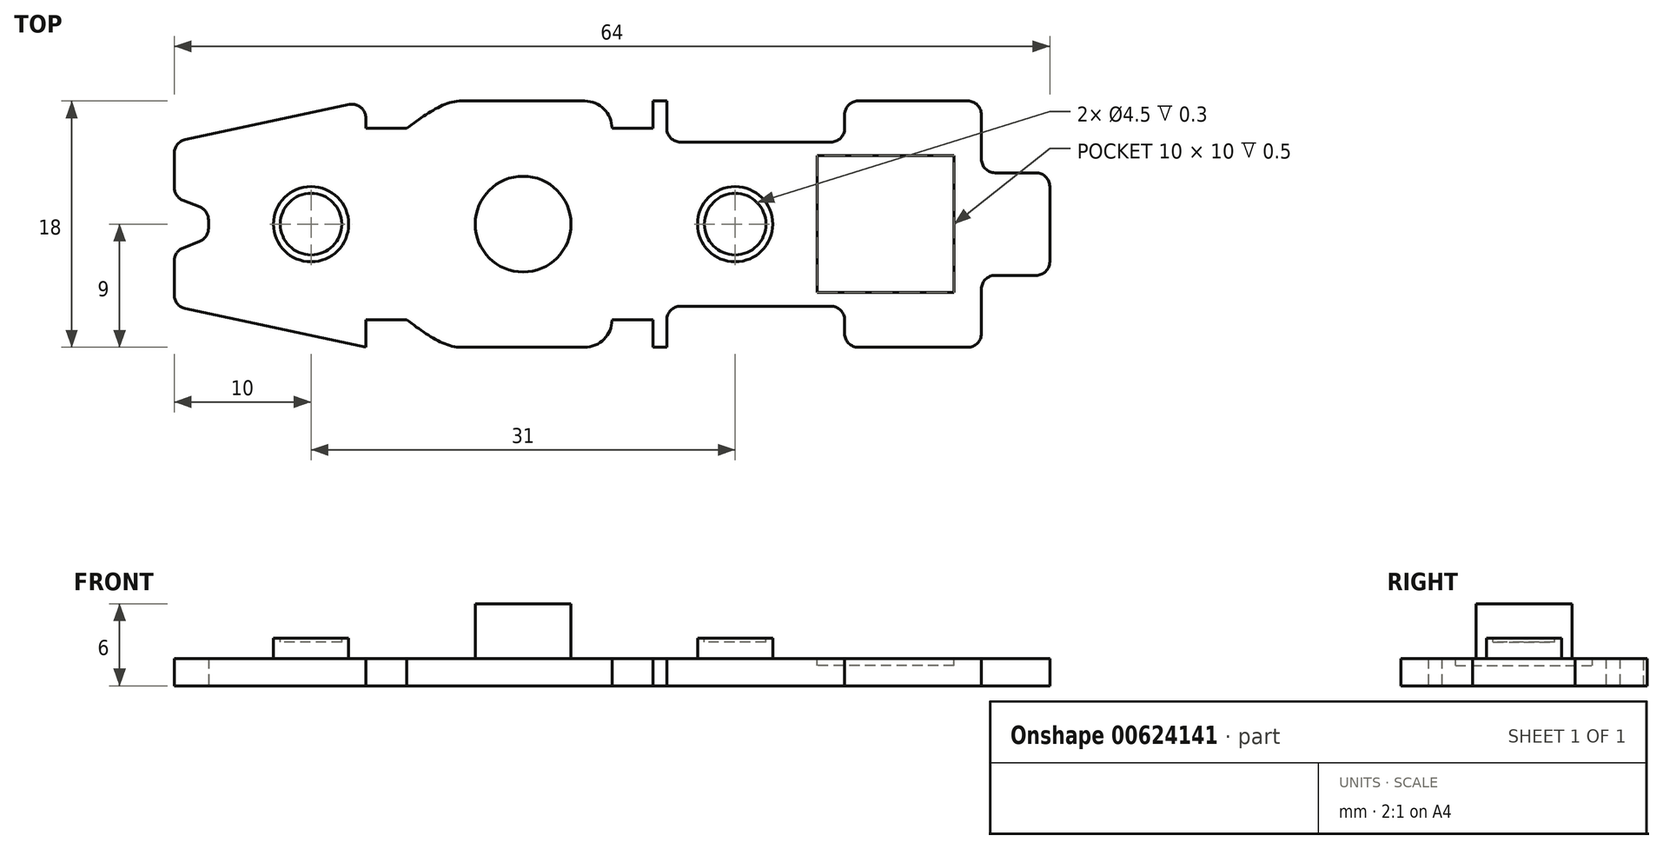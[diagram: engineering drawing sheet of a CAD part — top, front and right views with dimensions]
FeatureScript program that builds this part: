
annotation { "Feature Type Name" : "Feature", "Feature Type Description" : "" }
export const myFeature = defineFeature(function(context is Context, id is Id, definition is map)
    precondition{}
    {
        {
            var Q0;
            Q0=qCreatedBy(makeId("Top.planeOp"),FACE);
            var sketch = newSketch(context, id + "F0", { "sketchPlane" : qUnion([Q0])});
            skLineSegment(sketch, "E0.bottom", {"start": v(27, 9) * mm, "end": v(17, 9) * mm});
            skLineSegment(sketch, "E0.left", {"start": v(32, 3.75) * mm, "end": v(32, 0) * mm});
            skLineSegment(sketch, "E0.right", {"start": v(-32, 6) * mm, "end": v(-32, 2) * mm});
            skPoint(sketch, "E0.middle", {"position": v(0, 0) * mm});
            skLineSegment(sketch, "E1", {"start": v(32, 0) * mm, "end": v(32, 3.75) * mm});
            skLineSegment(sketch, "E2", {"start": v(32, 3.75) * mm, "end": v(28, 3.75) * mm});
            skLineSegment(sketch, "E3", {"start": v(27, 4.75) * mm, "end": v(27, 9) * mm});
            skPoint(sketch, "E4.orphan", {"position": v(32, 9) * mm});
            skLineSegment(sketch, "E5", {"start": v(17, 9) * mm, "end": v(17, 7) * mm});
            skLineSegment(sketch, "E6", {"start": v(16, 6) * mm, "end": v(5, 6) * mm});
            skLineSegment(sketch, "E7", {"start": v(4, 7) * mm, "end": v(4, 9) * mm});
            skLineSegment(sketch, "E8", {"start": v(4, 9) * mm, "end": v(3, 9) * mm});
            skLineSegment(sketch, "E9", {"start": v(3, 9) * mm, "end": v(3, 7) * mm});
            skLineSegment(sketch, "E10", {"start": v(3, 7) * mm, "end": v(0, 7) * mm});
            skPoint(sketch, "E11.start.orphan", {"position": v(-2, 7) * mm});
            skArc(sketch, "E12", {"start": v(-2, 9) * mm, "mid": v(-0.59, 8.41) * mm, "end": v(0, 7) * mm});
            skLineSegment(sketch, "E13.trimOffspring", {"start": v(-2, 9) * mm, "end": v(-11, 9) * mm});
            skPoint(sketch, "E14.orphan", {"position": v(0, 9) * mm});
            skFitSpline(sketch, "E15", {"points": [v(-15, 7) * mm, v(-11, 9) * mm, v(-7, 7) * mm], "startDerivative": vector(8, 6) * mm, "endDerivative": vector(8, -6) * mm});
            skLineSegment(sketch, "E16", {"start": v(-15, 7) * mm, "end": v(-18, 7) * mm});
            skLineSegment(sketch, "E17", {"start": v(-18, 7) * mm, "end": v(-18, 9) * mm});
            skLineSegment(sketch, "E18", {"start": v(-32, 2) * mm, "end": v(-32, 6) * mm});
            skLineSegment(sketch, "E19", {"start": v(-32, 6) * mm, "end": v(-18, 9) * mm});
            skLineSegment(sketch, "E20", {"start": v(-29.5, 0) * mm, "end": v(-29.5, 0.32) * mm});
            skLineSegment(sketch, "E21", {"start": v(-32, 2) * mm, "end": v(-30.13, 1.25) * mm});
            skPoint(sketch, "E22.orphan", {"position": v(-32, 9) * mm});
            skPoint(sketch, "E23.trimOffspring.start.orphan", {"position": v(-32, 0) * mm});
            skPoint(sketch, "E0.top.end.orphan", {"position": v(-32, -9) * mm});
            skPoint(sketch, "E24.orphan", {"position": v(32, -9) * mm});
            skLineSegment(sketch, "E25.MirrorCS", {"start": v(-29.5, 0) * mm, "end": v(-29.5, -0.32) * mm});
            skLineSegment(sketch, "E26.MirrorCS", {"start": v(-31.37, -1.75) * mm, "end": v(-30.13, -1.25) * mm});
            skLineSegment(sketch, "E27.MirrorCS", {"start": v(-32, -2.68) * mm, "end": v(-32, -5.2) * mm});
            skLineSegment(sketch, "E28.MirrorCS", {"start": v(-31.2, -6.17) * mm, "end": v(-18, -9) * mm});
            skLineSegment(sketch, "E29.MirrorCS", {"start": v(-18, -7) * mm, "end": v(-18, -9) * mm});
            skLineSegment(sketch, "E30.MirrorCS", {"start": v(-15, -7) * mm, "end": v(-18, -7) * mm});
            skFitSpline(sketch, "E31.MirrorCS", {"points": [v(-15, -7) * mm, v(-11, -9) * mm, v(-7, -7) * mm], "startDerivative": vector(8, -6) * mm, "endDerivative": vector(8, 6) * mm});
            skLineSegment(sketch, "E32.MirrorCS", {"start": v(-2, -9) * mm, "end": v(-11, -9) * mm});
            skArc(sketch, "E33.MirrorCS", {"start": v(-2, -9) * mm, "mid": v(-0.59, -8.41) * mm, "end": v(0, -7) * mm});
            skLineSegment(sketch, "E34.MirrorCS", {"start": v(3, -7) * mm, "end": v(0, -7) * mm});
            skLineSegment(sketch, "E35.MirrorCS", {"start": v(3, -9) * mm, "end": v(3, -7) * mm});
            skLineSegment(sketch, "E36.MirrorCS", {"start": v(4, -9) * mm, "end": v(3, -9) * mm});
            skLineSegment(sketch, "E37.MirrorCS", {"start": v(4, -7) * mm, "end": v(4, -9) * mm});
            skLineSegment(sketch, "E38.MirrorCS", {"start": v(16, -6) * mm, "end": v(5, -6) * mm});
            skLineSegment(sketch, "E39.MirrorCS", {"start": v(17, -8) * mm, "end": v(17, -7) * mm});
            skLineSegment(sketch, "E40.MirrorCS", {"start": v(26, -9) * mm, "end": v(18, -9) * mm});
            skLineSegment(sketch, "E41.MirrorCS", {"start": v(27, -4.75) * mm, "end": v(27, -8) * mm});
            skLineSegment(sketch, "E42.MirrorCS", {"start": v(32, -3.75) * mm, "end": v(28, -3.75) * mm});
            skLineSegment(sketch, "E43.MirrorCS", {"start": v(32, 0) * mm, "end": v(32, -3.75) * mm});
            skPoint(sketch, "E44.end.orphan", {"position": v(-29.5, 2) * mm});
            skPoint(sketch, "E45.visualSharp", {"position": v(27, 3.75) * mm});
            skArc(sketch, "E45.filletArc", {"start": v(27, 4.75) * mm, "mid": v(27.3, 4.04) * mm, "end": v(28, 3.75) * mm});
            skPoint(sketch, "E46.visualSharp", {"position": v(27, -3.75) * mm});
            skArc(sketch, "E46.filletArc", {"start": v(28, -3.75) * mm, "mid": v(27.3, -4.04) * mm, "end": v(27, -4.75) * mm});
            skPoint(sketch, "E47.visualSharp", {"position": v(-29.5, 1) * mm});
            skArc(sketch, "E47.filletArc", {"start": v(-29.5, 0.32) * mm, "mid": v(-29.67, 0.88) * mm, "end": v(-30.13, 1.25) * mm});
            skPoint(sketch, "E48.visualSharp", {"position": v(-29.5, -1) * mm});
            skArc(sketch, "E48.filletArc", {"start": v(-30.13, -1.25) * mm, "mid": v(-29.67, -0.88) * mm, "end": v(-29.5, -0.32) * mm});
            skPoint(sketch, "E49.visualSharp", {"position": v(-32, -2) * mm});
            skArc(sketch, "E49.filletArc", {"start": v(-31.37, -1.75) * mm, "mid": v(-31.83, -2.12) * mm, "end": v(-32, -2.68) * mm});
            skPoint(sketch, "E50.visualSharp", {"position": v(-32, -6) * mm});
            skArc(sketch, "E50.filletArc", {"start": v(-32, -5.2) * mm, "mid": v(-31.78, -5.82) * mm, "end": v(-31.2, -6.17) * mm});
            skPoint(sketch, "E51.visualSharp", {"position": v(4, 6) * mm});
            skArc(sketch, "E51.filletArc", {"start": v(4, 7) * mm, "mid": v(4.3, 6.3) * mm, "end": v(5, 6) * mm});
            skPoint(sketch, "E52.visualSharp", {"position": v(4, -6) * mm});
            skArc(sketch, "E52.filletArc", {"start": v(5, -6) * mm, "mid": v(4.3, -6.3) * mm, "end": v(4, -7) * mm});
            skPoint(sketch, "E53.visualSharp", {"position": v(17, -6) * mm});
            skArc(sketch, "E53.filletArc", {"start": v(17, -7) * mm, "mid": v(16.7, -6.3) * mm, "end": v(16, -6) * mm});
            skPoint(sketch, "E54.visualSharp", {"position": v(17, 6) * mm});
            skArc(sketch, "E54.filletArc", {"start": v(16, 6) * mm, "mid": v(16.7, 6.3) * mm, "end": v(17, 7) * mm});
            skPoint(sketch, "E55.visualSharp", {"position": v(17, -9) * mm});
            skArc(sketch, "E55.filletArc", {"start": v(17, -8) * mm, "mid": v(17.3, -8.7) * mm, "end": v(18, -9) * mm});
            skPoint(sketch, "E56.visualSharp", {"position": v(27, -9) * mm});
            skArc(sketch, "E56.filletArc", {"start": v(26, -9) * mm, "mid": v(26.7, -8.7) * mm, "end": v(27, -8) * mm});
            skSolve(sketch);
        }
        {
            var Q0;
            Q0 = qSketchRegion(id + "F0", true);
            extrude(context, id + "F1", {"entities" : qUnion([Q0]), "depth" : 2 * mm, "offsetDistance" : 25 * mm});
        }
        {
            var Q0;
            Q0=makeQuery(id+"F1.opExtrude","SWEPT_EDGE",EDGE,{"disambiguationData":[OSD([sQuery(id+"F0.wireOp",EDGE,"E18"),sQuery(id+"F0.wireOp",EDGE,"E21")])]});
            var Q1;
            Q1=makeQuery(id+"F1.opExtrude","SWEPT_EDGE",EDGE,{"disambiguationData":[OSD([sQuery(id+"F0.wireOp",EDGE,"E18"),sQuery(id+"F0.wireOp",EDGE,"E19")])]});
            var Q2;
            Q2=makeQuery(id+"F1.opExtrude","SWEPT_EDGE",EDGE,{"disambiguationData":[OSD([sQuery(id+"F0.wireOp",EDGE,"E3"),sQuery(id+"F0.wireOp",EDGE,"E0.bottom")])]});
            var Q3;
            Q3=makeQuery(id+"F1.opExtrude","SWEPT_EDGE",EDGE,{"disambiguationData":[OSD([sQuery(id+"F0.wireOp",EDGE,"E0.bottom"),sQuery(id+"F0.wireOp",EDGE,"E5")])]});
            var Q4;
            Q4=makeQuery(id+"F1.opExtrude","SWEPT_EDGE",EDGE,{"disambiguationData":[OSD([sQuery(id+"F0.wireOp",EDGE,"E42.MirrorCS"),sQuery(id+"F0.wireOp",EDGE,"E43.MirrorCS")])]});
            var Q5;
            Q5=makeQuery(id+"F1.opExtrude","SWEPT_EDGE",EDGE,{"disambiguationData":[OSD([sQuery(id+"F0.wireOp",EDGE,"E1"),sQuery(id+"F0.wireOp",EDGE,"E2")])]});
            fillet(context, id + "F2", {"entities" : qUnion([Q0, Q1, Q2, Q3, Q4, Q5]), "radius" : 1 * mm, "tangentPropagation" : true, "allowEdgeOverflow" : false});
        }
        {
            var Q0;
            Q0=makeQuery(id+"F1.opExtrude","CAP_FACE",FACE,{"disambiguationData":[OSD([sQuery(id+"F0.wireOp",EDGE,"E1"),sQuery(id+"F0.wireOp",EDGE,"E2"),sQuery(id+"F0.wireOp",EDGE,"E3"),sQuery(id+"F0.wireOp",EDGE,"E0.bottom"),sQuery(id+"F0.wireOp",EDGE,"E5"),sQuery(id+"F0.wireOp",EDGE,"E6"),sQuery(id+"F0.wireOp",EDGE,"E7"),sQuery(id+"F0.wireOp",EDGE,"E8"),sQuery(id+"F0.wireOp",EDGE,"E9"),sQuery(id+"F0.wireOp",EDGE,"E10"),sQuery(id+"F0.wireOp",EDGE,"E12"),sQuery(id+"F0.wireOp",EDGE,"E13.trimOffspring"),sQuery(id+"F0.wireOp",EDGE,"E15"),sQuery(id+"F0.wireOp",EDGE,"E16"),sQuery(id+"F0.wireOp",EDGE,"E17"),sQuery(id+"F0.wireOp",EDGE,"E18"),sQuery(id+"F0.wireOp",EDGE,"E19"),sQuery(id+"F0.wireOp",EDGE,"E20"),sQuery(id+"F0.wireOp",EDGE,"E21"),sQuery(id+"F0.wireOp",EDGE,"E25.MirrorCS"),sQuery(id+"F0.wireOp",EDGE,"E26.MirrorCS"),sQuery(id+"F0.wireOp",EDGE,"E27.MirrorCS"),sQuery(id+"F0.wireOp",EDGE,"E28.MirrorCS"),sQuery(id+"F0.wireOp",EDGE,"E29.MirrorCS"),sQuery(id+"F0.wireOp",EDGE,"E30.MirrorCS"),sQuery(id+"F0.wireOp",EDGE,"E31.MirrorCS"),sQuery(id+"F0.wireOp",EDGE,"E32.MirrorCS"),sQuery(id+"F0.wireOp",EDGE,"E33.MirrorCS"),sQuery(id+"F0.wireOp",EDGE,"E34.MirrorCS"),sQuery(id+"F0.wireOp",EDGE,"E35.MirrorCS"),sQuery(id+"F0.wireOp",EDGE,"E36.MirrorCS"),sQuery(id+"F0.wireOp",EDGE,"E37.MirrorCS"),sQuery(id+"F0.wireOp",EDGE,"E38.MirrorCS"),sQuery(id+"F0.wireOp",EDGE,"E39.MirrorCS"),sQuery(id+"F0.wireOp",EDGE,"E40.MirrorCS"),sQuery(id+"F0.wireOp",EDGE,"E41.MirrorCS"),sQuery(id+"F0.wireOp",EDGE,"E42.MirrorCS"),sQuery(id+"F0.wireOp",EDGE,"E43.MirrorCS"),sQuery(id+"F0.wireOp",EDGE,"E45.filletArc"),sQuery(id+"F0.wireOp",EDGE,"E46.filletArc"),sQuery(id+"F0.wireOp",EDGE,"E47.filletArc"),sQuery(id+"F0.wireOp",EDGE,"E48.filletArc"),sQuery(id+"F0.wireOp",EDGE,"E49.filletArc"),sQuery(id+"F0.wireOp",EDGE,"E50.filletArc"),sQuery(id+"F0.wireOp",EDGE,"E51.filletArc"),sQuery(id+"F0.wireOp",EDGE,"E52.filletArc"),sQuery(id+"F0.wireOp",EDGE,"E53.filletArc"),sQuery(id+"F0.wireOp",EDGE,"E54.filletArc"),sQuery(id+"F0.wireOp",EDGE,"E55.filletArc"),sQuery(id+"F0.wireOp",EDGE,"E56.filletArc")])],"isStart":false});
            var sketch = newSketch(context, id + "F3", { "sketchPlane" : qUnion([Q0])});
            skLineSegment(sketch, "E57", {"start": v(32, 0) * mm, "end": v(25, 0) * mm});
            skPoint(sketch, "E57.endSnap0", {"position": v(32, 0) * mm});
            skLineSegment(sketch, "E58", {"start": v(25, 0) * mm, "end": v(25, 5) * mm});
            skLineSegment(sketch, "E59", {"start": v(25, 5) * mm, "end": v(15, 5) * mm});
            skLineSegment(sketch, "E60", {"start": v(15, 5) * mm, "end": v(15, -5) * mm});
            skLineSegment(sketch, "E61", {"start": v(15, -5) * mm, "end": v(25, -5) * mm});
            skLineSegment(sketch, "E62", {"start": v(25, -5) * mm, "end": v(25, 0) * mm});
            skSolve(sketch);
        }
        {
            var Q0;
            Q0 = qSketchRegion(id + "F3", true);
            extrude(context, id + "F4", {"entities" : qUnion([Q0]), "operationType" : NewBodyOperationType.REMOVE, "oppositeDirection" : true, "depth" : 0.5 * mm, "offsetDistance" : 25 * mm});
        }
        {
            var Q0;
            Q0=makeQuery(id+"F1.opExtrude","CAP_FACE",FACE,{"disambiguationData":[OSD([sQuery(id+"F0.wireOp",EDGE,"E1"),sQuery(id+"F0.wireOp",EDGE,"E2"),sQuery(id+"F0.wireOp",EDGE,"E3"),sQuery(id+"F0.wireOp",EDGE,"E0.bottom"),sQuery(id+"F0.wireOp",EDGE,"E5"),sQuery(id+"F0.wireOp",EDGE,"E6"),sQuery(id+"F0.wireOp",EDGE,"E7"),sQuery(id+"F0.wireOp",EDGE,"E8"),sQuery(id+"F0.wireOp",EDGE,"E9"),sQuery(id+"F0.wireOp",EDGE,"E10"),sQuery(id+"F0.wireOp",EDGE,"E12"),sQuery(id+"F0.wireOp",EDGE,"E13.trimOffspring"),sQuery(id+"F0.wireOp",EDGE,"E15"),sQuery(id+"F0.wireOp",EDGE,"E16"),sQuery(id+"F0.wireOp",EDGE,"E17"),sQuery(id+"F0.wireOp",EDGE,"E18"),sQuery(id+"F0.wireOp",EDGE,"E19"),sQuery(id+"F0.wireOp",EDGE,"E20"),sQuery(id+"F0.wireOp",EDGE,"E21"),sQuery(id+"F0.wireOp",EDGE,"E25.MirrorCS"),sQuery(id+"F0.wireOp",EDGE,"E26.MirrorCS"),sQuery(id+"F0.wireOp",EDGE,"E27.MirrorCS"),sQuery(id+"F0.wireOp",EDGE,"E28.MirrorCS"),sQuery(id+"F0.wireOp",EDGE,"E29.MirrorCS"),sQuery(id+"F0.wireOp",EDGE,"E30.MirrorCS"),sQuery(id+"F0.wireOp",EDGE,"E31.MirrorCS"),sQuery(id+"F0.wireOp",EDGE,"E32.MirrorCS"),sQuery(id+"F0.wireOp",EDGE,"E33.MirrorCS"),sQuery(id+"F0.wireOp",EDGE,"E34.MirrorCS"),sQuery(id+"F0.wireOp",EDGE,"E35.MirrorCS"),sQuery(id+"F0.wireOp",EDGE,"E36.MirrorCS"),sQuery(id+"F0.wireOp",EDGE,"E37.MirrorCS"),sQuery(id+"F0.wireOp",EDGE,"E38.MirrorCS"),sQuery(id+"F0.wireOp",EDGE,"E39.MirrorCS"),sQuery(id+"F0.wireOp",EDGE,"E40.MirrorCS"),sQuery(id+"F0.wireOp",EDGE,"E41.MirrorCS"),sQuery(id+"F0.wireOp",EDGE,"E42.MirrorCS"),sQuery(id+"F0.wireOp",EDGE,"E43.MirrorCS"),sQuery(id+"F0.wireOp",EDGE,"E45.filletArc"),sQuery(id+"F0.wireOp",EDGE,"E46.filletArc"),sQuery(id+"F0.wireOp",EDGE,"E47.filletArc"),sQuery(id+"F0.wireOp",EDGE,"E48.filletArc"),sQuery(id+"F0.wireOp",EDGE,"E49.filletArc"),sQuery(id+"F0.wireOp",EDGE,"E50.filletArc"),sQuery(id+"F0.wireOp",EDGE,"E51.filletArc"),sQuery(id+"F0.wireOp",EDGE,"E52.filletArc"),sQuery(id+"F0.wireOp",EDGE,"E53.filletArc"),sQuery(id+"F0.wireOp",EDGE,"E54.filletArc"),sQuery(id+"F0.wireOp",EDGE,"E55.filletArc"),sQuery(id+"F0.wireOp",EDGE,"E56.filletArc")])],"isStart":false});
            var sketch = newSketch(context, id + "F5", { "sketchPlane" : qUnion([Q0])});
            skLineSegment(sketch, "E63", {"start": v(32, 0) * mm, "end": v(9, 0) * mm});
            skCircle(sketch, "E64", {"center": v(9, 0) * mm, "radius": 2.75 * mm});
            skLineSegment(sketch, "E65", {"start": v(6.25, 0) * mm, "end": v(-6.5, 0) * mm});
            skCircle(sketch, "E66", {"center": v(-6.5, 0) * mm, "radius": 3.5 * mm});
            skLineSegment(sketch, "E67", {"start": v(-10, 0) * mm, "end": v(-22, 0) * mm});
            skCircle(sketch, "E68", {"center": v(-22, 0) * mm, "radius": 2.75 * mm});
            skSolve(sketch);
        }
        {
            var Q0;
            Q0 = qSketchRegion(id + "F5", true);
            extrude(context, id + "F6", {"entities" : qUnion([Q0]), "operationType" : NewBodyOperationType.ADD, "depth" : 1.5 * mm, "offsetDistance" : 25 * mm});
        }
        {
            var Q0;
            Q0=makeQuery(id+"F6.opExtrude","CAP_FACE",FACE,{"disambiguationData":[OSD([sQuery(id+"F5.wireOp",EDGE,"E64")])],"isStart":false});
            var sketch = newSketch(context, id + "F7", { "sketchPlane" : qUnion([Q0])});
            skCircle(sketch, "E69", {"center": v(9, 0) * mm, "radius": 2.25 * mm});
            skCircle(sketch, "E70", {"center": v(-22, 0) * mm, "radius": 2.25 * mm});
            skSolve(sketch);
        }
        {
            var Q0;
            Q0 = qSketchRegion(id + "F7", true);
            extrude(context, id + "F8", {"entities" : qUnion([Q0]), "operationType" : NewBodyOperationType.REMOVE, "oppositeDirection" : true, "depth" : 0.3 * mm, "offsetDistance" : 25 * mm});
        }
        {
            var Q0;
            Q0=makeQuery(id+"F6.opExtrude","CAP_FACE",FACE,{"disambiguationData":[OSD([sQuery(id+"F5.wireOp",EDGE,"E66")])],"isStart":false});
            var sketch = newSketch(context, id + "F9", { "sketchPlane" : qUnion([Q0])});
            skCircle(sketch, "E71.0.0", {"center": v(-6.5, 0) * mm, "radius": 3.5 * mm});
            skSolve(sketch);
        }
        {
            var Q0;
            Q0 = qSketchRegion(id + "F9", true);
            extrude(context, id + "F10", {"entities" : qUnion([Q0]), "operationType" : NewBodyOperationType.ADD, "depth" : 2.5 * mm, "offsetDistance" : 25 * mm});
        }
    });
